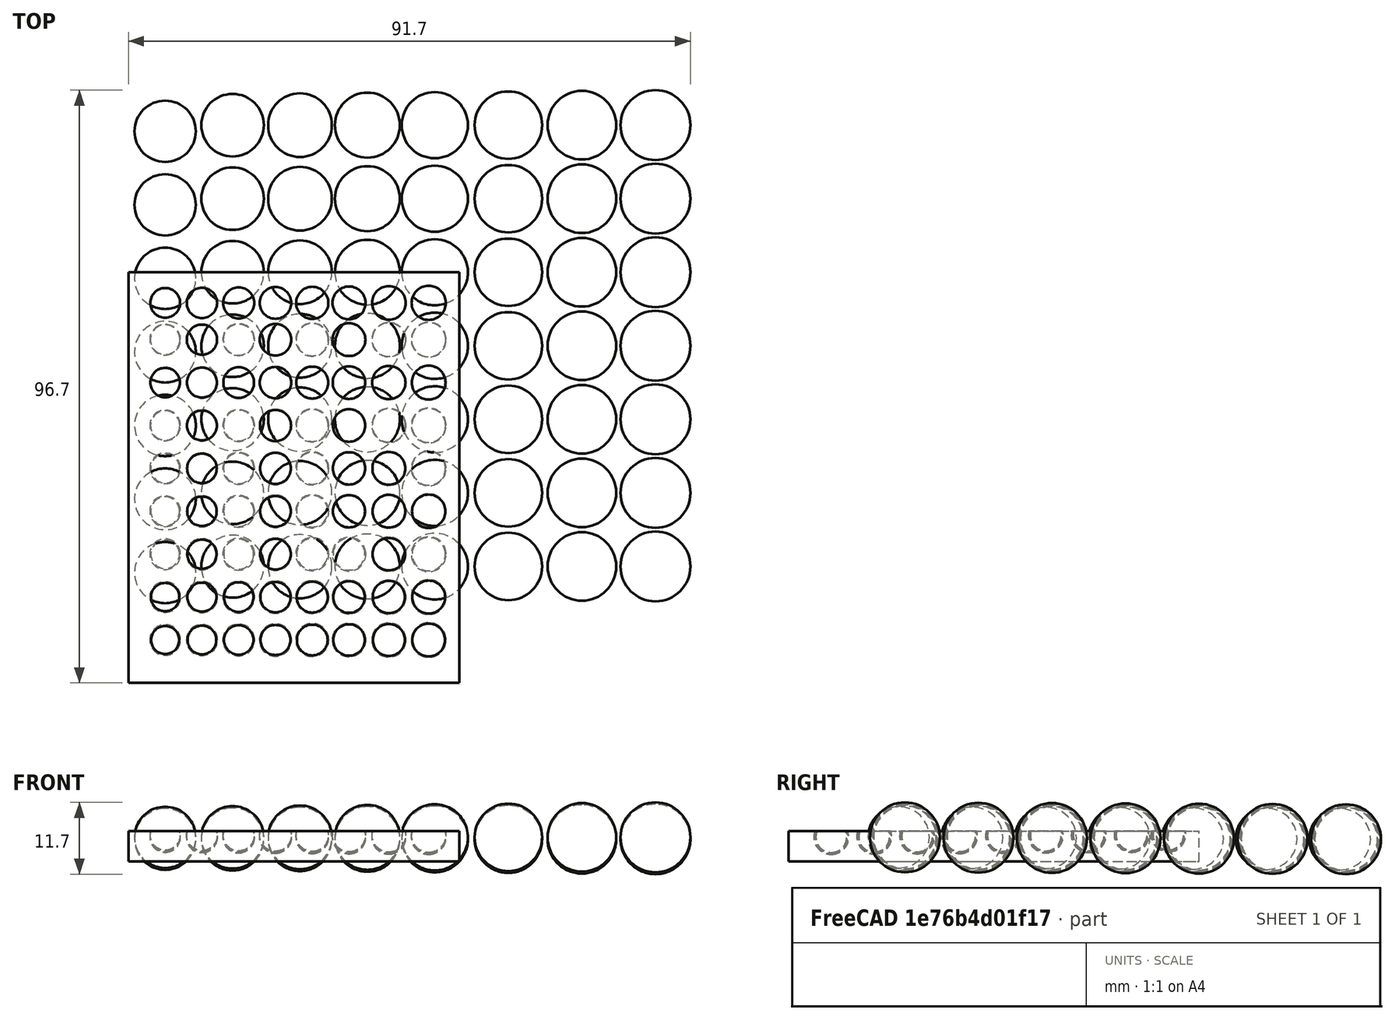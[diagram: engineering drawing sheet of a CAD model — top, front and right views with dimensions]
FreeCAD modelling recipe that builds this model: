
FCSTD DOCUMENT  (FreeCAD 0.17R13522 (Git))
Label: Ball Magnet plate
License: All rights reserved
LicenseURL: http://en.wikipedia.org/wiki/All_rights_reserved
objects: Part::Sphere×135, Part::MultiFuse×17, Part::Box×1, App::DocumentObjectGroup×1, Part::Cut×1
note: 154 computed .brp shape members not serialized (recipe doc carries the construction recipe); baked Part::Feature solids carry a one-line shape summary decoded from their .brp

FEATURE [Part::Box] Box001  label="Cube001"
  AttacherType = Attacher::AttachEngine3D
  Height = 5
  Length = 54
  Placement = pos=(1,0,3) rot=(0,0,1;0rad)
  Width = 67
FEATURE [Part::Sphere] Sphere
  Angle1 = -90
  Angle2 = 90
  Angle3 = 360
  AttacherType = Attacher::AttachEngine3D
  Placement = pos=(7,7,7) rot=(0,0,1;0rad)
  Radius = 2.5
FEATURE [Part::Sphere] Sphere001
  Angle1 = -90
  Angle2 = 90
  Angle3 = 360
  AttacherType = Attacher::AttachEngine3D
  Placement = pos=(13,7,7) rot=(0,0,1;0rad)
  Radius = 2.55
FEATURE [Part::Sphere] Sphere002
  Angle1 = -90
  Angle2 = 90
  Angle3 = 360
  AttacherType = Attacher::AttachEngine3D
  Placement = pos=(19,7,7) rot=(0,0,1;0rad)
  Radius = 2.6
FEATURE [Part::Sphere] Sphere003
  Angle1 = -90
  Angle2 = 90
  Angle3 = 360
  AttacherType = Attacher::AttachEngine3D
  Placement = pos=(25,7,7) rot=(0,0,1;0rad)
  Radius = 2.65
FEATURE [Part::Sphere] Sphere004
  Angle1 = -90
  Angle2 = 90
  Angle3 = 360
  AttacherType = Attacher::AttachEngine3D
  Placement = pos=(31,7,7) rot=(0,0,1;0rad)
  Radius = 2.7
FEATURE [Part::Sphere] Sphere005
  Angle1 = -90
  Angle2 = 90
  Angle3 = 360
  AttacherType = Attacher::AttachEngine3D
  Placement = pos=(37,7,7) rot=(0,0,1;0rad)
  Radius = 2.75
FEATURE [Part::Sphere] Sphere006
  Angle1 = -90
  Angle2 = 90
  Angle3 = 360
  AttacherType = Attacher::AttachEngine3D
  Placement = pos=(43.5,7,7) rot=(0,0,1;0rad)
  Radius = 2.8
FEATURE [Part::Sphere] Sphere007
  Angle1 = -90
  Angle2 = 90
  Angle3 = 360
  AttacherType = Attacher::AttachEngine3D
  Placement = pos=(50,7,7) rot=(0,0,1;0rad)
  Radius = 2.85
FEATURE [Part::Sphere] Sphere008
  Angle1 = -90
  Angle2 = 90
  Angle3 = 360
  AttacherType = Attacher::AttachEngine3D
  Placement = pos=(7,18,6.95) rot=(0,0,1;0rad)
  Radius = 5
FEATURE [Part::Sphere] Sphere009
  Angle1 = -90
  Angle2 = 90
  Angle3 = 360
  AttacherType = Attacher::AttachEngine3D
  Placement = pos=(7,18,6.95) rot=(0,0,1;0rad)
  Radius = 5
FEATURE [Part::Sphere] Sphere010
  Angle1 = -90
  Angle2 = 90
  Angle3 = 360
  AttacherType = Attacher::AttachEngine3D
  Placement = pos=(18,19,6.95) rot=(0,0,1;0rad)
  Radius = 5.1
FEATURE [Part::Sphere] Sphere011
  Angle1 = -90
  Angle2 = 90
  Angle3 = 360
  AttacherType = Attacher::AttachEngine3D
  Placement = pos=(29,19,6.95) rot=(0,0,1;0rad)
  Radius = 5.2
FEATURE [Part::Sphere] Sphere012
  Angle1 = -90
  Angle2 = 90
  Angle3 = 360
  AttacherType = Attacher::AttachEngine3D
  Placement = pos=(51,19,6.95) rot=(0,0,1;0rad)
  Radius = 5.4
FEATURE [Part::Sphere] Sphere013
  Angle1 = -90
  Angle2 = 90
  Angle3 = 360
  AttacherType = Attacher::AttachEngine3D
  Placement = pos=(40,19,6.95) rot=(0,0,1;0rad)
  Radius = 5.3
FEATURE [Part::Sphere] Sphere014
  Angle1 = -90
  Angle2 = 90
  Angle3 = 360
  AttacherType = Attacher::AttachEngine3D
  Placement = pos=(75,19,6.95) rot=(0,0,1;0rad)
  Radius = 5.6
FEATURE [Part::Sphere] Sphere015
  Angle1 = -90
  Angle2 = 90
  Angle3 = 360
  AttacherType = Attacher::AttachEngine3D
  Placement = pos=(63,19,6.95) rot=(0,0,1;0rad)
  Radius = 5.5
FEATURE [Part::Sphere] Sphere016
  Angle1 = -90
  Angle2 = 90
  Angle3 = 360
  AttacherType = Attacher::AttachEngine3D
  Placement = pos=(87,19,6.95) rot=(0,0,1;0rad)
  Radius = 5.7
FEATURE [Part::MultiFuse] Fusion
  Shapes = -> [Sphere008,Sphere014,Sphere010,Sphere013,Sphere011,Sphere015,Sphere012,Sphere016,Sphere009]
FEATURE [Part::Sphere] Sphere017
  Angle1 = -90
  Angle2 = 90
  Angle3 = 360
  AttacherType = Attacher::AttachEngine3D
  Placement = pos=(75,19,6.95) rot=(0,0,1;0rad)
  Radius = 5.6
FEATURE [Part::Sphere] Sphere018
  Angle1 = -90
  Angle2 = 90
  Angle3 = 360
  AttacherType = Attacher::AttachEngine3D
  Placement = pos=(18,19,6.95) rot=(0,0,1;0rad)
  Radius = 5.1
FEATURE [Part::Sphere] Sphere019
  Angle1 = -90
  Angle2 = 90
  Angle3 = 360
  AttacherType = Attacher::AttachEngine3D
  Placement = pos=(40,19,6.95) rot=(0,0,1;0rad)
  Radius = 5.3
FEATURE [Part::Sphere] Sphere020
  Angle1 = -90
  Angle2 = 90
  Angle3 = 360
  AttacherType = Attacher::AttachEngine3D
  Placement = pos=(7,18,6.95) rot=(0,0,1;0rad)
  Radius = 5
FEATURE [Part::Sphere] Sphere021
  Angle1 = -90
  Angle2 = 90
  Angle3 = 360
  AttacherType = Attacher::AttachEngine3D
  Placement = pos=(29,19,6.95) rot=(0,0,1;0rad)
  Radius = 5.2
FEATURE [Part::Sphere] Sphere022
  Angle1 = -90
  Angle2 = 90
  Angle3 = 360
  AttacherType = Attacher::AttachEngine3D
  Placement = pos=(63,19,6.95) rot=(0,0,1;0rad)
  Radius = 5.5
FEATURE [Part::Sphere] Sphere023
  Angle1 = -90
  Angle2 = 90
  Angle3 = 360
  AttacherType = Attacher::AttachEngine3D
  Placement = pos=(51,19,6.95) rot=(0,0,1;0rad)
  Radius = 5.4
FEATURE [Part::Sphere] Sphere024
  Angle1 = -90
  Angle2 = 90
  Angle3 = 360
  AttacherType = Attacher::AttachEngine3D
  Placement = pos=(87,19,6.95) rot=(0,0,1;0rad)
  Radius = 5.7
FEATURE [Part::Sphere] Sphere025
  Angle1 = -90
  Angle2 = 90
  Angle3 = 360
  AttacherType = Attacher::AttachEngine3D
  Placement = pos=(7,18,6.95) rot=(0,0,1;0rad)
  Radius = 5
FEATURE [Part::MultiFuse] Fusion001
  Placement = pos=(0,12,-0.05) rot=(0,0,1;0rad)
  Shapes = -> [Sphere020,Sphere017,Sphere018,Sphere019,Sphere021,Sphere022,Sphere023,Sphere024,Sphere025]
FEATURE [Part::Sphere] Sphere026
  Angle1 = -90
  Angle2 = 90
  Angle3 = 360
  AttacherType = Attacher::AttachEngine3D
  Placement = pos=(75,19,6.95) rot=(0,0,1;0rad)
  Radius = 5.6
FEATURE [Part::Sphere] Sphere027
  Angle1 = -90
  Angle2 = 90
  Angle3 = 360
  AttacherType = Attacher::AttachEngine3D
  Placement = pos=(40,19,6.95) rot=(0,0,1;0rad)
  Radius = 5.3
FEATURE [Part::Sphere] Sphere028
  Angle1 = -90
  Angle2 = 90
  Angle3 = 360
  AttacherType = Attacher::AttachEngine3D
  Placement = pos=(7,18,6.95) rot=(0,0,1;0rad)
  Radius = 5
FEATURE [Part::Sphere] Sphere029
  Angle1 = -90
  Angle2 = 90
  Angle3 = 360
  AttacherType = Attacher::AttachEngine3D
  Placement = pos=(29,19,6.95) rot=(0,0,1;0rad)
  Radius = 5.2
FEATURE [Part::Sphere] Sphere030
  Angle1 = -90
  Angle2 = 90
  Angle3 = 360
  AttacherType = Attacher::AttachEngine3D
  Placement = pos=(63,19,6.95) rot=(0,0,1;0rad)
  Radius = 5.5
FEATURE [Part::Sphere] Sphere031
  Angle1 = -90
  Angle2 = 90
  Angle3 = 360
  AttacherType = Attacher::AttachEngine3D
  Placement = pos=(51,19,6.95) rot=(0,0,1;0rad)
  Radius = 5.4
FEATURE [Part::Sphere] Sphere032
  Angle1 = -90
  Angle2 = 90
  Angle3 = 360
  AttacherType = Attacher::AttachEngine3D
  Placement = pos=(87,19,6.95) rot=(0,0,1;0rad)
  Radius = 5.7
FEATURE [Part::Sphere] Sphere033
  Angle1 = -90
  Angle2 = 90
  Angle3 = 360
  AttacherType = Attacher::AttachEngine3D
  Placement = pos=(7,18,6.95) rot=(0,0,1;0rad)
  Radius = 5
FEATURE [Part::Sphere] Sphere034
  Angle1 = -90
  Angle2 = 90
  Angle3 = 360
  AttacherType = Attacher::AttachEngine3D
  Placement = pos=(18,19,6.95) rot=(0,0,1;0rad)
  Radius = 5.1
FEATURE [Part::MultiFuse] Fusion002
  Placement = pos=(0,24,-0.1) rot=(0,0,1;0rad)
  Shapes = -> [Sphere028,Sphere026,Sphere034,Sphere027,Sphere029,Sphere030,Sphere031,Sphere032,Sphere033]
FEATURE [Part::Sphere] Sphere035
  Angle1 = -90
  Angle2 = 90
  Angle3 = 360
  AttacherType = Attacher::AttachEngine3D
  Placement = pos=(63,19,6.95) rot=(0,0,1;0rad)
  Radius = 5.5
FEATURE [Part::Sphere] Sphere036
  Angle1 = -90
  Angle2 = 90
  Angle3 = 360
  AttacherType = Attacher::AttachEngine3D
  Placement = pos=(7,18,6.95) rot=(0,0,1;0rad)
  Radius = 5
FEATURE [Part::Sphere] Sphere037
  Angle1 = -90
  Angle2 = 90
  Angle3 = 360
  AttacherType = Attacher::AttachEngine3D
  Placement = pos=(51,19,6.95) rot=(0,0,1;0rad)
  Radius = 5.4
FEATURE [Part::Sphere] Sphere038
  Angle1 = -90
  Angle2 = 90
  Angle3 = 360
  AttacherType = Attacher::AttachEngine3D
  Placement = pos=(40,19,6.95) rot=(0,0,1;0rad)
  Radius = 5.3
FEATURE [Part::Sphere] Sphere039
  Angle1 = -90
  Angle2 = 90
  Angle3 = 360
  AttacherType = Attacher::AttachEngine3D
  Placement = pos=(29,19,6.95) rot=(0,0,1;0rad)
  Radius = 5.2
FEATURE [Part::Sphere] Sphere040
  Angle1 = -90
  Angle2 = 90
  Angle3 = 360
  AttacherType = Attacher::AttachEngine3D
  Placement = pos=(7,18,6.95) rot=(0,0,1;0rad)
  Radius = 5
FEATURE [Part::Sphere] Sphere041
  Angle1 = -90
  Angle2 = 90
  Angle3 = 360
  AttacherType = Attacher::AttachEngine3D
  Placement = pos=(87,19,6.95) rot=(0,0,1;0rad)
  Radius = 5.7
FEATURE [Part::Sphere] Sphere042
  Angle1 = -90
  Angle2 = 90
  Angle3 = 360
  AttacherType = Attacher::AttachEngine3D
  Placement = pos=(75,19,6.95) rot=(0,0,1;0rad)
  Radius = 5.6
FEATURE [Part::Sphere] Sphere043
  Angle1 = -90
  Angle2 = 90
  Angle3 = 360
  AttacherType = Attacher::AttachEngine3D
  Placement = pos=(18,19,6.95) rot=(0,0,1;0rad)
  Radius = 5.1
FEATURE [Part::MultiFuse] Fusion003
  Placement = pos=(0,36,-0.15) rot=(0,0,1;0rad)
  Shapes = -> [Sphere040,Sphere042,Sphere043,Sphere038,Sphere039,Sphere035,Sphere037,Sphere041,Sphere036]
FEATURE [Part::Sphere] Sphere044
  Angle1 = -90
  Angle2 = 90
  Angle3 = 360
  AttacherType = Attacher::AttachEngine3D
  Placement = pos=(63,19,6.95) rot=(0,0,1;0rad)
  Radius = 5.5
FEATURE [Part::Sphere] Sphere045
  Angle1 = -90
  Angle2 = 90
  Angle3 = 360
  AttacherType = Attacher::AttachEngine3D
  Placement = pos=(7,18,6.95) rot=(0,0,1;0rad)
  Radius = 5
FEATURE [Part::Sphere] Sphere046
  Angle1 = -90
  Angle2 = 90
  Angle3 = 360
  AttacherType = Attacher::AttachEngine3D
  Placement = pos=(29,19,6.95) rot=(0,0,1;0rad)
  Radius = 5.2
FEATURE [Part::Sphere] Sphere047
  Angle1 = -90
  Angle2 = 90
  Angle3 = 360
  AttacherType = Attacher::AttachEngine3D
  Placement = pos=(7,18,6.95) rot=(0,0,1;0rad)
  Radius = 5
FEATURE [Part::Sphere] Sphere048
  Angle1 = -90
  Angle2 = 90
  Angle3 = 360
  AttacherType = Attacher::AttachEngine3D
  Placement = pos=(51,19,6.95) rot=(0,0,1;0rad)
  Radius = 5.4
FEATURE [Part::Sphere] Sphere049
  Angle1 = -90
  Angle2 = 90
  Angle3 = 360
  AttacherType = Attacher::AttachEngine3D
  Placement = pos=(40,19,6.95) rot=(0,0,1;0rad)
  Radius = 5.3
FEATURE [Part::Sphere] Sphere050
  Angle1 = -90
  Angle2 = 90
  Angle3 = 360
  AttacherType = Attacher::AttachEngine3D
  Placement = pos=(87,19,6.95) rot=(0,0,1;0rad)
  Radius = 5.7
FEATURE [Part::Sphere] Sphere051
  Angle1 = -90
  Angle2 = 90
  Angle3 = 360
  AttacherType = Attacher::AttachEngine3D
  Placement = pos=(75,19,6.95) rot=(0,0,1;0rad)
  Radius = 5.6
FEATURE [Part::Sphere] Sphere052
  Angle1 = -90
  Angle2 = 90
  Angle3 = 360
  AttacherType = Attacher::AttachEngine3D
  Placement = pos=(18,19,6.95) rot=(0,0,1;0rad)
  Radius = 5.1
FEATURE [Part::MultiFuse] Fusion004
  Placement = pos=(0,48,-0.2) rot=(0,0,1;0rad)
  Shapes = -> [Sphere047,Sphere051,Sphere052,Sphere049,Sphere046,Sphere044,Sphere048,Sphere050,Sphere045]
FEATURE [Part::Sphere] Sphere053
  Angle1 = -90
  Angle2 = 90
  Angle3 = 360
  AttacherType = Attacher::AttachEngine3D
  Placement = pos=(7,18,6.95) rot=(0,0,1;0rad)
  Radius = 5
FEATURE [Part::Sphere] Sphere054
  Angle1 = -90
  Angle2 = 90
  Angle3 = 360
  AttacherType = Attacher::AttachEngine3D
  Placement = pos=(29,19,6.95) rot=(0,0,1;0rad)
  Radius = 5.2
FEATURE [Part::Sphere] Sphere055
  Angle1 = -90
  Angle2 = 90
  Angle3 = 360
  AttacherType = Attacher::AttachEngine3D
  Placement = pos=(40,19,6.95) rot=(0,0,1;0rad)
  Radius = 5.3
FEATURE [Part::Sphere] Sphere056
  Angle1 = -90
  Angle2 = 90
  Angle3 = 360
  AttacherType = Attacher::AttachEngine3D
  Placement = pos=(63,19,6.95) rot=(0,0,1;0rad)
  Radius = 5.5
FEATURE [Part::Sphere] Sphere057
  Angle1 = -90
  Angle2 = 90
  Angle3 = 360
  AttacherType = Attacher::AttachEngine3D
  Placement = pos=(7,18,6.95) rot=(0,0,1;0rad)
  Radius = 5
FEATURE [Part::Sphere] Sphere058
  Angle1 = -90
  Angle2 = 90
  Angle3 = 360
  AttacherType = Attacher::AttachEngine3D
  Placement = pos=(51,19,6.95) rot=(0,0,1;0rad)
  Radius = 5.4
FEATURE [Part::Sphere] Sphere059
  Angle1 = -90
  Angle2 = 90
  Angle3 = 360
  AttacherType = Attacher::AttachEngine3D
  Placement = pos=(87,19,6.95) rot=(0,0,1;0rad)
  Radius = 5.7
FEATURE [Part::Sphere] Sphere060
  Angle1 = -90
  Angle2 = 90
  Angle3 = 360
  AttacherType = Attacher::AttachEngine3D
  Placement = pos=(75,19,6.95) rot=(0,0,1;0rad)
  Radius = 5.6
FEATURE [Part::Sphere] Sphere061
  Angle1 = -90
  Angle2 = 90
  Angle3 = 360
  AttacherType = Attacher::AttachEngine3D
  Placement = pos=(18,19,6.95) rot=(0,0,1;0rad)
  Radius = 5.1
FEATURE [Part::MultiFuse] Fusion005
  Placement = pos=(0,60,-0.25) rot=(0,0,1;0rad)
  Shapes = -> [Sphere053,Sphere060,Sphere061,Sphere055,Sphere054,Sphere056,Sphere058,Sphere059,Sphere057]
FEATURE [Part::Sphere] Sphere062
  Angle1 = -90
  Angle2 = 90
  Angle3 = 360
  AttacherType = Attacher::AttachEngine3D
  Placement = pos=(7,18,6.95) rot=(0,0,1;0rad)
  Radius = 5
FEATURE [Part::Sphere] Sphere063
  Angle1 = -90
  Angle2 = 90
  Angle3 = 360
  AttacherType = Attacher::AttachEngine3D
  Placement = pos=(63,19,6.95) rot=(0,0,1;0rad)
  Radius = 5.5
FEATURE [Part::Sphere] Sphere064
  Angle1 = -90
  Angle2 = 90
  Angle3 = 360
  AttacherType = Attacher::AttachEngine3D
  Placement = pos=(87,19,6.95) rot=(0,0,1;0rad)
  Radius = 5.7
FEATURE [Part::Sphere] Sphere065
  Angle1 = -90
  Angle2 = 90
  Angle3 = 360
  AttacherType = Attacher::AttachEngine3D
  Placement = pos=(75,19,6.95) rot=(0,0,1;0rad)
  Radius = 5.6
FEATURE [Part::Sphere] Sphere066
  Angle1 = -90
  Angle2 = 90
  Angle3 = 360
  AttacherType = Attacher::AttachEngine3D
  Placement = pos=(18,19,6.95) rot=(0,0,1;0rad)
  Radius = 5.1
FEATURE [Part::Sphere] Sphere067
  Angle1 = -90
  Angle2 = 90
  Angle3 = 360
  AttacherType = Attacher::AttachEngine3D
  Placement = pos=(29,19,6.95) rot=(0,0,1;0rad)
  Radius = 5.2
FEATURE [Part::Sphere] Sphere068
  Angle1 = -90
  Angle2 = 90
  Angle3 = 360
  AttacherType = Attacher::AttachEngine3D
  Placement = pos=(7,18,6.95) rot=(0,0,1;0rad)
  Radius = 5
FEATURE [Part::Sphere] Sphere069
  Angle1 = -90
  Angle2 = 90
  Angle3 = 360
  AttacherType = Attacher::AttachEngine3D
  Placement = pos=(40,19,6.95) rot=(0,0,1;0rad)
  Radius = 5.3
FEATURE [Part::Sphere] Sphere070
  Angle1 = -90
  Angle2 = 90
  Angle3 = 360
  AttacherType = Attacher::AttachEngine3D
  Placement = pos=(51,19,6.95) rot=(0,0,1;0rad)
  Radius = 5.4
FEATURE [Part::MultiFuse] Fusion006
  Placement = pos=(0,72,-0.3) rot=(0,0,1;0rad)
  Shapes = -> [Sphere068,Sphere065,Sphere066,Sphere069,Sphere067,Sphere063,Sphere070,Sphere064,Sphere062]
FEATURE [Part::MultiFuse] Fusion007
  Shapes = -> [Sphere,Sphere001,Sphere004,Sphere006,Sphere002,Sphere007,Sphere003,Sphere005]
FEATURE [App::DocumentObjectGroup] Group
  Group = -> [Fusion,Fusion002,Fusion001,Fusion003,Fusion004,Fusion005,Fusion006]
FEATURE [Part::Sphere] Sphere071
  Angle1 = -90
  Angle2 = 90
  Angle3 = 360
  AttacherType = Attacher::AttachEngine3D
  Placement = pos=(19,7,7) rot=(0,0,1;0rad)
  Radius = 2.6
FEATURE [Part::Sphere] Sphere072
  Angle1 = -90
  Angle2 = 90
  Angle3 = 360
  AttacherType = Attacher::AttachEngine3D
  Placement = pos=(7,7,7) rot=(0,0,1;0rad)
  Radius = 2.5
FEATURE [Part::Sphere] Sphere073
  Angle1 = -90
  Angle2 = 90
  Angle3 = 360
  AttacherType = Attacher::AttachEngine3D
  Placement = pos=(13,7,7) rot=(0,0,1;0rad)
  Radius = 2.55
FEATURE [Part::Sphere] Sphere074
  Angle1 = -90
  Angle2 = 90
  Angle3 = 360
  AttacherType = Attacher::AttachEngine3D
  Placement = pos=(25,7,7) rot=(0,0,1;0rad)
  Radius = 2.65
FEATURE [Part::Sphere] Sphere075
  Angle1 = -90
  Angle2 = 90
  Angle3 = 360
  AttacherType = Attacher::AttachEngine3D
  Placement = pos=(31,7,7) rot=(0,0,1;0rad)
  Radius = 2.7
FEATURE [Part::Sphere] Sphere076
  Angle1 = -90
  Angle2 = 90
  Angle3 = 360
  AttacherType = Attacher::AttachEngine3D
  Placement = pos=(37,7,7) rot=(0,0,1;0rad)
  Radius = 2.75
FEATURE [Part::Sphere] Sphere077
  Angle1 = -90
  Angle2 = 90
  Angle3 = 360
  AttacherType = Attacher::AttachEngine3D
  Placement = pos=(43.5,7,7) rot=(0,0,1;0rad)
  Radius = 2.8
FEATURE [Part::Sphere] Sphere078
  Angle1 = -90
  Angle2 = 90
  Angle3 = 360
  AttacherType = Attacher::AttachEngine3D
  Placement = pos=(50,7,7) rot=(0,0,1;0rad)
  Radius = 2.85
FEATURE [Part::MultiFuse] Fusion008
  Placement = pos=(0,7,0.05) rot=(0,0,1;0rad)
  Shapes = -> [Sphere072,Sphere073,Sphere075,Sphere077,Sphere071,Sphere078,Sphere074,Sphere076]
FEATURE [Part::Sphere] Sphere079
  Angle1 = -90
  Angle2 = 90
  Angle3 = 360
  AttacherType = Attacher::AttachEngine3D
  Placement = pos=(25,7,7) rot=(0,0,1;0rad)
  Radius = 2.65
FEATURE [Part::Sphere] Sphere080
  Angle1 = -90
  Angle2 = 90
  Angle3 = 360
  AttacherType = Attacher::AttachEngine3D
  Placement = pos=(31,7,7) rot=(0,0,1;0rad)
  Radius = 2.7
FEATURE [Part::Sphere] Sphere081
  Angle1 = -90
  Angle2 = 90
  Angle3 = 360
  AttacherType = Attacher::AttachEngine3D
  Placement = pos=(13,7,7) rot=(0,0,1;0rad)
  Radius = 2.55
FEATURE [Part::Sphere] Sphere082
  Angle1 = -90
  Angle2 = 90
  Angle3 = 360
  AttacherType = Attacher::AttachEngine3D
  Placement = pos=(19,7,7) rot=(0,0,1;0rad)
  Radius = 2.6
FEATURE [Part::Sphere] Sphere083
  Angle1 = -90
  Angle2 = 90
  Angle3 = 360
  AttacherType = Attacher::AttachEngine3D
  Placement = pos=(7,7,7) rot=(0,0,1;0rad)
  Radius = 2.5
FEATURE [Part::Sphere] Sphere084
  Angle1 = -90
  Angle2 = 90
  Angle3 = 360
  AttacherType = Attacher::AttachEngine3D
  Placement = pos=(43.5,7,7) rot=(0,0,1;0rad)
  Radius = 2.8
FEATURE [Part::Sphere] Sphere085
  Angle1 = -90
  Angle2 = 90
  Angle3 = 360
  AttacherType = Attacher::AttachEngine3D
  Placement = pos=(50,7,7) rot=(0,0,1;0rad)
  Radius = 2.85
FEATURE [Part::Sphere] Sphere086
  Angle1 = -90
  Angle2 = 90
  Angle3 = 360
  AttacherType = Attacher::AttachEngine3D
  Placement = pos=(37,7,7) rot=(0,0,1;0rad)
  Radius = 2.75
FEATURE [Part::MultiFuse] Fusion009
  Placement = pos=(0,14,0.1) rot=(0,0,1;0rad)
  Shapes = -> [Sphere083,Sphere081,Sphere080,Sphere084,Sphere082,Sphere085,Sphere079,Sphere086]
FEATURE [Part::Sphere] Sphere087
  Angle1 = -90
  Angle2 = 90
  Angle3 = 360
  AttacherType = Attacher::AttachEngine3D
  Placement = pos=(37,7,7) rot=(0,0,1;0rad)
  Radius = 2.75
FEATURE [Part::Sphere] Sphere088
  Angle1 = -90
  Angle2 = 90
  Angle3 = 360
  AttacherType = Attacher::AttachEngine3D
  Placement = pos=(25,7,7) rot=(0,0,1;0rad)
  Radius = 2.65
FEATURE [Part::Sphere] Sphere089
  Angle1 = -90
  Angle2 = 90
  Angle3 = 360
  AttacherType = Attacher::AttachEngine3D
  Placement = pos=(7,7,7) rot=(0,0,1;0rad)
  Radius = 2.5
FEATURE [Part::Sphere] Sphere090
  Angle1 = -90
  Angle2 = 90
  Angle3 = 360
  AttacherType = Attacher::AttachEngine3D
  Placement = pos=(31,7,7) rot=(0,0,1;0rad)
  Radius = 2.7
FEATURE [Part::Sphere] Sphere091
  Angle1 = -90
  Angle2 = 90
  Angle3 = 360
  AttacherType = Attacher::AttachEngine3D
  Placement = pos=(43.5,7,7) rot=(0,0,1;0rad)
  Radius = 2.8
FEATURE [Part::Sphere] Sphere092
  Angle1 = -90
  Angle2 = 90
  Angle3 = 360
  AttacherType = Attacher::AttachEngine3D
  Placement = pos=(13,7,7) rot=(0,0,1;0rad)
  Radius = 2.55
FEATURE [Part::Sphere] Sphere093
  Angle1 = -90
  Angle2 = 90
  Angle3 = 360
  AttacherType = Attacher::AttachEngine3D
  Placement = pos=(19,7,7) rot=(0,0,1;0rad)
  Radius = 2.6
FEATURE [Part::Sphere] Sphere094
  Angle1 = -90
  Angle2 = 90
  Angle3 = 360
  AttacherType = Attacher::AttachEngine3D
  Placement = pos=(50,7,7) rot=(0,0,1;0rad)
  Radius = 2.85
FEATURE [Part::MultiFuse] Fusion010
  Placement = pos=(0,21,0.15) rot=(0,0,1;0rad)
  Shapes = -> [Sphere089,Sphere092,Sphere090,Sphere091,Sphere093,Sphere094,Sphere088,Sphere087]
FEATURE [Part::Sphere] Sphere095
  Angle1 = -90
  Angle2 = 90
  Angle3 = 360
  AttacherType = Attacher::AttachEngine3D
  Placement = pos=(25,7,7) rot=(0,0,1;0rad)
  Radius = 2.65
FEATURE [Part::Sphere] Sphere096
  Angle1 = -90
  Angle2 = 90
  Angle3 = 360
  AttacherType = Attacher::AttachEngine3D
  Placement = pos=(7,7,7) rot=(0,0,1;0rad)
  Radius = 2.5
FEATURE [Part::Sphere] Sphere097
  Angle1 = -90
  Angle2 = 90
  Angle3 = 360
  AttacherType = Attacher::AttachEngine3D
  Placement = pos=(37,7,7) rot=(0,0,1;0rad)
  Radius = 2.75
FEATURE [Part::Sphere] Sphere098
  Angle1 = -90
  Angle2 = 90
  Angle3 = 360
  AttacherType = Attacher::AttachEngine3D
  Placement = pos=(31,7,7) rot=(0,0,1;0rad)
  Radius = 2.7
FEATURE [Part::Sphere] Sphere099
  Angle1 = -90
  Angle2 = 90
  Angle3 = 360
  AttacherType = Attacher::AttachEngine3D
  Placement = pos=(13,7,7) rot=(0,0,1;0rad)
  Radius = 2.55
FEATURE [Part::Sphere] Sphere100
  Angle1 = -90
  Angle2 = 90
  Angle3 = 360
  AttacherType = Attacher::AttachEngine3D
  Placement = pos=(43.5,7,7) rot=(0,0,1;0rad)
  Radius = 2.8
FEATURE [Part::Sphere] Sphere101
  Angle1 = -90
  Angle2 = 90
  Angle3 = 360
  AttacherType = Attacher::AttachEngine3D
  Placement = pos=(19,7,7) rot=(0,0,1;0rad)
  Radius = 2.6
FEATURE [Part::Sphere] Sphere102
  Angle1 = -90
  Angle2 = 90
  Angle3 = 360
  AttacherType = Attacher::AttachEngine3D
  Placement = pos=(50,7,7) rot=(0,0,1;0rad)
  Radius = 2.85
FEATURE [Part::MultiFuse] Fusion011
  Placement = pos=(0,28,0.2) rot=(0,0,1;0rad)
  Shapes = -> [Sphere096,Sphere099,Sphere098,Sphere100,Sphere101,Sphere102,Sphere095,Sphere097]
FEATURE [Part::Sphere] Sphere103
  Angle1 = -90
  Angle2 = 90
  Angle3 = 360
  AttacherType = Attacher::AttachEngine3D
  Placement = pos=(25,7,7) rot=(0,0,1;0rad)
  Radius = 2.65
FEATURE [Part::Sphere] Sphere104
  Angle1 = -90
  Angle2 = 90
  Angle3 = 360
  AttacherType = Attacher::AttachEngine3D
  Placement = pos=(31,7,7) rot=(0,0,1;0rad)
  Radius = 2.7
FEATURE [Part::Sphere] Sphere105
  Angle1 = -90
  Angle2 = 90
  Angle3 = 360
  AttacherType = Attacher::AttachEngine3D
  Placement = pos=(37,7,7) rot=(0,0,1;0rad)
  Radius = 2.75
FEATURE [Part::Sphere] Sphere106
  Angle1 = -90
  Angle2 = 90
  Angle3 = 360
  AttacherType = Attacher::AttachEngine3D
  Placement = pos=(13,7,7) rot=(0,0,1;0rad)
  Radius = 2.55
FEATURE [Part::Sphere] Sphere107
  Angle1 = -90
  Angle2 = 90
  Angle3 = 360
  AttacherType = Attacher::AttachEngine3D
  Placement = pos=(43.5,7,7) rot=(0,0,1;0rad)
  Radius = 2.8
FEATURE [Part::Sphere] Sphere108
  Angle1 = -90
  Angle2 = 90
  Angle3 = 360
  AttacherType = Attacher::AttachEngine3D
  Placement = pos=(7,7,7) rot=(0,0,1;0rad)
  Radius = 2.5
FEATURE [Part::Sphere] Sphere109
  Angle1 = -90
  Angle2 = 90
  Angle3 = 360
  AttacherType = Attacher::AttachEngine3D
  Placement = pos=(19,7,7) rot=(0,0,1;0rad)
  Radius = 2.6
FEATURE [Part::Sphere] Sphere110
  Angle1 = -90
  Angle2 = 90
  Angle3 = 360
  AttacherType = Attacher::AttachEngine3D
  Placement = pos=(50,7,7) rot=(0,0,1;0rad)
  Radius = 2.85
FEATURE [Part::MultiFuse] Fusion012
  Placement = pos=(0,35,0.25) rot=(0,0,1;0rad)
  Shapes = -> [Sphere108,Sphere106,Sphere104,Sphere107,Sphere109,Sphere110,Sphere103,Sphere105]
FEATURE [Part::Sphere] Sphere111
  Angle1 = -90
  Angle2 = 90
  Angle3 = 360
  AttacherType = Attacher::AttachEngine3D
  Placement = pos=(13,7,7) rot=(0,0,1;0rad)
  Radius = 2.55
FEATURE [Part::Sphere] Sphere112
  Angle1 = -90
  Angle2 = 90
  Angle3 = 360
  AttacherType = Attacher::AttachEngine3D
  Placement = pos=(43.5,7,7) rot=(0,0,1;0rad)
  Radius = 2.8
FEATURE [Part::Sphere] Sphere113
  Angle1 = -90
  Angle2 = 90
  Angle3 = 360
  AttacherType = Attacher::AttachEngine3D
  Placement = pos=(7,7,7) rot=(0,0,1;0rad)
  Radius = 2.5
FEATURE [Part::Sphere] Sphere114
  Angle1 = -90
  Angle2 = 90
  Angle3 = 360
  AttacherType = Attacher::AttachEngine3D
  Placement = pos=(19,7,7) rot=(0,0,1;0rad)
  Radius = 2.6
FEATURE [Part::Sphere] Sphere115
  Angle1 = -90
  Angle2 = 90
  Angle3 = 360
  AttacherType = Attacher::AttachEngine3D
  Placement = pos=(50,7,7) rot=(0,0,1;0rad)
  Radius = 2.85
FEATURE [Part::Sphere] Sphere116
  Angle1 = -90
  Angle2 = 90
  Angle3 = 360
  AttacherType = Attacher::AttachEngine3D
  Placement = pos=(37,7,7) rot=(0,0,1;0rad)
  Radius = 2.75
FEATURE [Part::Sphere] Sphere117
  Angle1 = -90
  Angle2 = 90
  Angle3 = 360
  AttacherType = Attacher::AttachEngine3D
  Placement = pos=(31,7,7) rot=(0,0,1;0rad)
  Radius = 2.7
FEATURE [Part::Sphere] Sphere118
  Angle1 = -90
  Angle2 = 90
  Angle3 = 360
  AttacherType = Attacher::AttachEngine3D
  Placement = pos=(25,7,7) rot=(0,0,1;0rad)
  Radius = 2.65
FEATURE [Part::MultiFuse] Fusion013
  Placement = pos=(0,42,0.3) rot=(0,0,1;0rad)
  Shapes = -> [Sphere113,Sphere111,Sphere117,Sphere112,Sphere114,Sphere115,Sphere118,Sphere116]
FEATURE [Part::Sphere] Sphere119
  Angle1 = -90
  Angle2 = 90
  Angle3 = 360
  AttacherType = Attacher::AttachEngine3D
  Placement = pos=(13,7,7) rot=(0,0,1;0rad)
  Radius = 2.55
FEATURE [Part::Sphere] Sphere120
  Angle1 = -90
  Angle2 = 90
  Angle3 = 360
  AttacherType = Attacher::AttachEngine3D
  Placement = pos=(19,7,7) rot=(0,0,1;0rad)
  Radius = 2.6
FEATURE [Part::Sphere] Sphere121
  Angle1 = -90
  Angle2 = 90
  Angle3 = 360
  AttacherType = Attacher::AttachEngine3D
  Placement = pos=(50,7,7) rot=(0,0,1;0rad)
  Radius = 2.85
FEATURE [Part::Sphere] Sphere122
  Angle1 = -90
  Angle2 = 90
  Angle3 = 360
  AttacherType = Attacher::AttachEngine3D
  Placement = pos=(43.5,7,7) rot=(0,0,1;0rad)
  Radius = 2.8
FEATURE [Part::Sphere] Sphere123
  Angle1 = -90
  Angle2 = 90
  Angle3 = 360
  AttacherType = Attacher::AttachEngine3D
  Placement = pos=(7,7,7) rot=(0,0,1;0rad)
  Radius = 2.5
FEATURE [Part::Sphere] Sphere124
  Angle1 = -90
  Angle2 = 90
  Angle3 = 360
  AttacherType = Attacher::AttachEngine3D
  Placement = pos=(37,7,7) rot=(0,0,1;0rad)
  Radius = 2.75
FEATURE [Part::Sphere] Sphere125
  Angle1 = -90
  Angle2 = 90
  Angle3 = 360
  AttacherType = Attacher::AttachEngine3D
  Placement = pos=(31,7,7) rot=(0,0,1;0rad)
  Radius = 2.7
FEATURE [Part::Sphere] Sphere126
  Angle1 = -90
  Angle2 = 90
  Angle3 = 360
  AttacherType = Attacher::AttachEngine3D
  Placement = pos=(25,7,7) rot=(0,0,1;0rad)
  Radius = 2.65
FEATURE [Part::MultiFuse] Fusion014
  Placement = pos=(0,49,0.35) rot=(0,0,1;0rad)
  Shapes = -> [Sphere123,Sphere119,Sphere125,Sphere122,Sphere120,Sphere121,Sphere126,Sphere124]
FEATURE [Part::Sphere] Sphere127
  Angle1 = -90
  Angle2 = 90
  Angle3 = 360
  AttacherType = Attacher::AttachEngine3D
  Placement = pos=(19,7,7) rot=(0,0,1;0rad)
  Radius = 2.6
FEATURE [Part::Sphere] Sphere128
  Angle1 = -90
  Angle2 = 90
  Angle3 = 360
  AttacherType = Attacher::AttachEngine3D
  Placement = pos=(13,7,7) rot=(0,0,1;0rad)
  Radius = 2.55
FEATURE [Part::Sphere] Sphere129
  Angle1 = -90
  Angle2 = 90
  Angle3 = 360
  AttacherType = Attacher::AttachEngine3D
  Placement = pos=(50,7,7) rot=(0,0,1;0rad)
  Radius = 2.85
FEATURE [Part::Sphere] Sphere130
  Angle1 = -90
  Angle2 = 90
  Angle3 = 360
  AttacherType = Attacher::AttachEngine3D
  Placement = pos=(43.5,7,7) rot=(0,0,1;0rad)
  Radius = 2.8
FEATURE [Part::Sphere] Sphere131
  Angle1 = -90
  Angle2 = 90
  Angle3 = 360
  AttacherType = Attacher::AttachEngine3D
  Placement = pos=(7,7,7) rot=(0,0,1;0rad)
  Radius = 2.5
FEATURE [Part::Sphere] Sphere132
  Angle1 = -90
  Angle2 = 90
  Angle3 = 360
  AttacherType = Attacher::AttachEngine3D
  Placement = pos=(37,7,7) rot=(0,0,1;0rad)
  Radius = 2.75
FEATURE [Part::Sphere] Sphere133
  Angle1 = -90
  Angle2 = 90
  Angle3 = 360
  AttacherType = Attacher::AttachEngine3D
  Placement = pos=(31,7,7) rot=(0,0,1;0rad)
  Radius = 2.7
FEATURE [Part::Sphere] Sphere134
  Angle1 = -90
  Angle2 = 90
  Angle3 = 360
  AttacherType = Attacher::AttachEngine3D
  Placement = pos=(25,7,7) rot=(0,0,1;0rad)
  Radius = 2.65
FEATURE [Part::MultiFuse] Fusion015
  Placement = pos=(0,55,0.4) rot=(0,0,1;0rad)
  Shapes = -> [Sphere131,Sphere128,Sphere133,Sphere130,Sphere127,Sphere129,Sphere134,Sphere132]
FEATURE [Part::MultiFuse] Fusion016
  Shapes = -> [Fusion007,Fusion008,Fusion009,Fusion010,Fusion011,Fusion012,Fusion014,Fusion013,Fusion015]
FEATURE [Part::Cut] Cut
  Base = -> Box001
  Tool = -> Fusion016
